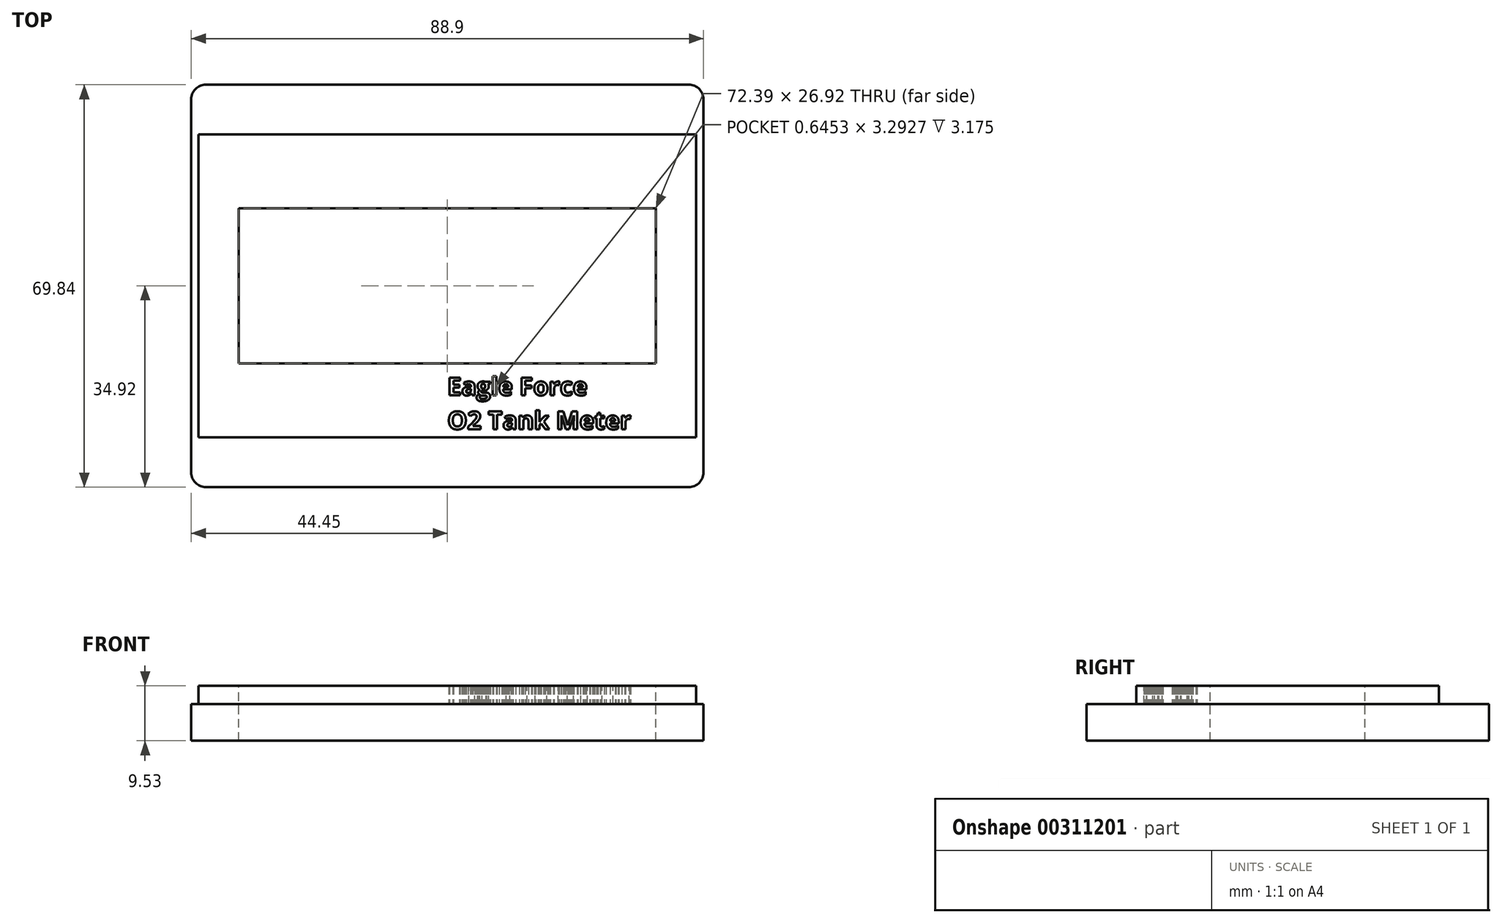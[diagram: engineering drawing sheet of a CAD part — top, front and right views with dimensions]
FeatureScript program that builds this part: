
annotation { "Feature Type Name" : "Feature", "Feature Type Description" : "" }
export const myFeature = defineFeature(function(context is Context, id is Id, definition is map)
    precondition{}
    {
        {
            var Q0;
            Q0=qCreatedBy(makeId("Top.planeOp"),FACE);
            var sketch = newSketch(context, id + "F0", { "sketchPlane" : qUnion([Q0])});
            skLineSegment(sketch, "E0.bottom", {"start": v(-44.45, 34.93) * mm, "end": v(44.45, 34.93) * mm});
            skLineSegment(sketch, "E0.top", {"start": v(-44.45, -34.93) * mm, "end": v(44.45, -34.93) * mm});
            skLineSegment(sketch, "E0.left", {"start": v(-44.45, 34.93) * mm, "end": v(-44.45, -34.93) * mm});
            skLineSegment(sketch, "E0.right", {"start": v(44.45, 34.93) * mm, "end": v(44.45, -34.93) * mm});
            skPoint(sketch, "E0.middle", {"position": v(0, 0) * mm});
            skSolve(sketch);
        }
        {
            var Q0;
            Q0 = qSketchRegion(id + "F0", true);
            extrude(context, id + "F1", {"entities" : qUnion([Q0]), "depth" : 6.35 * mm});
        }
        {
            var Q0;
            Q0=makeQuery(id+"F1.opExtrude","CAP_FACE",FACE,{"disambiguationData":[OSD([sQuery(id+"F0.wireOp",EDGE,"E0.bottom"),sQuery(id+"F0.wireOp",EDGE,"E0.top"),sQuery(id+"F0.wireOp",EDGE,"E0.left"),sQuery(id+"F0.wireOp",EDGE,"E0.right")])],"isStart":false});
            var sketch = newSketch(context, id + "F2", { "sketchPlane" : qUnion([Q0])});
            skLineSegment(sketch, "E1", {"start": v(0, 0) * mm, "end": v(-38.8, 0) * mm});
            skLineSegment(sketch, "E2", {"start": v(-38.8, 0) * mm, "end": v(-38.8, 16.79) * mm});
            skSolve(sketch);
        }
        {
            var Q0;
            Q0=makeQuery(id+"F1.opExtrude","SWEPT_BODY",BODY,{"disambiguationData":[OSD([sQuery(id+"F0.wireOp",EDGE,"E0.bottom"),sQuery(id+"F0.wireOp",EDGE,"E0.top"),sQuery(id+"F0.wireOp",EDGE,"E0.left"),sQuery(id+"F0.wireOp",EDGE,"E0.right")])]});
            var Q1;
            Q1=qCreatedBy(makeId("Front.planeOp"),FACE);
            mirror(context, id + "F3", {"operationType" : NewBodyOperationType.ADD, "entities" : qUnion([Q0]), "mirrorPlane" : qUnion([Q1])});
        }
        {
            var Q0;
            Q0=makeQuery(id+"F1.opExtrude","SWEPT_BODY",BODY,{"disambiguationData":[OSD([sQuery(id+"F0.wireOp",EDGE,"E0.bottom"),sQuery(id+"F0.wireOp",EDGE,"E0.top"),sQuery(id+"F0.wireOp",EDGE,"E0.left"),sQuery(id+"F0.wireOp",EDGE,"E0.right")])]});
            var Q1;
            Q1=qCreatedBy(makeId("Right.planeOp"),FACE);
            mirror(context, id + "F4", {"operationType" : NewBodyOperationType.ADD, "entities" : qUnion([Q0]), "mirrorPlane" : qUnion([Q1])});
        }
        {
            var Q0;
            Q0=makeQuery(id+"F2.imprint","IMPRINT",FACE,{"disambiguationData":[TD([[makeQuery(id+"F2.imprint","IMPRINT",EDGE,{"derivedFrom":makeQuery(id+"F1.opExtrude","CAP_EDGE",EDGE,{"disambiguationData":[OSD([sQuery(id+"F0.wireOp",EDGE,"E0.bottom")])],"isStart":false})}),-1.0]])]});
            var sketch = newSketch(context, id + "F5", { "sketchPlane" : qUnion([Q0])});
            skLineSegment(sketch, "E3.bottom", {"start": v(-36.2, 13.46) * mm, "end": v(36.2, 13.46) * mm});
            skLineSegment(sketch, "E3.top", {"start": v(-36.2, -13.46) * mm, "end": v(36.2, -13.46) * mm});
            skLineSegment(sketch, "E3.left", {"start": v(-36.2, 13.46) * mm, "end": v(-36.2, -13.46) * mm});
            skLineSegment(sketch, "E3.right", {"start": v(36.2, 13.46) * mm, "end": v(36.2, -13.46) * mm});
            skPoint(sketch, "E3.middle", {"position": v(0, 0) * mm});
            skSolve(sketch);
        }
        {
            var Q0;
            Q0=makeQuery(id+"F1.opExtrude","SWEPT_EDGE",EDGE,{"disambiguationData":[OSD([sQuery(id+"F0.wireOp",EDGE,"E0.bottom"),sQuery(id+"F0.wireOp",EDGE,"E0.right")])]});
            var Q1;
            Q1=makeQuery(id+"F1.opExtrude","SWEPT_EDGE",EDGE,{"disambiguationData":[OSD([sQuery(id+"F0.wireOp",EDGE,"E0.bottom"),sQuery(id+"F0.wireOp",EDGE,"E0.left")])]});
            var Q2;
            Q2=makeQuery(id+"F1.opExtrude","SWEPT_EDGE",EDGE,{"disambiguationData":[OSD([sQuery(id+"F0.wireOp",EDGE,"E0.top"),sQuery(id+"F0.wireOp",EDGE,"E0.left")])]});
            var Q3;
            Q3=makeQuery(id+"F1.opExtrude","SWEPT_EDGE",EDGE,{"disambiguationData":[OSD([sQuery(id+"F0.wireOp",EDGE,"E0.top"),sQuery(id+"F0.wireOp",EDGE,"E0.right")])]});
            fillet(context, id + "F6", {"entities" : qUnion([Q0, Q1, Q2, Q3]), "radius" : 2.54 * mm, "tangentPropagation" : true, "allowEdgeOverflow" : false});
        }
        {
            var Q0;
            Q0=makeQuery(id+"F2.imprint","IMPRINT",FACE,{"disambiguationData":[TD([[makeQuery(id+"F2.imprint","IMPRINT",EDGE,{"derivedFrom":makeQuery(id+"F1.opExtrude","CAP_EDGE",EDGE,{"disambiguationData":[OSD([sQuery(id+"F0.wireOp",EDGE,"E0.bottom")])],"isStart":false})}),-1.0]])]});
            var sketch = newSketch(context, id + "F7", { "sketchPlane" : qUnion([Q0])});
            skLineSegment(sketch, "E4.bottom", {"start": v(43.18, 26.28) * mm, "end": v(-43.18, 26.28) * mm});
            skLineSegment(sketch, "E4.top", {"start": v(43.18, -26.28) * mm, "end": v(-43.18, -26.28) * mm});
            skLineSegment(sketch, "E4.left", {"start": v(43.18, 26.28) * mm, "end": v(43.18, -26.28) * mm});
            skLineSegment(sketch, "E4.right", {"start": v(-43.18, 26.28) * mm, "end": v(-43.18, -26.28) * mm});
            skPoint(sketch, "E4.middle", {"position": v(0, 0) * mm});
            skSolve(sketch);
        }
        {
            var Q0;
            Q0 = qSketchRegion(id + "F7", true);
            extrude(context, id + "F8", {"entities" : qUnion([Q0]), "operationType" : NewBodyOperationType.ADD, "depth" : 3.17 * mm});
        }
        {
            var Q0;
            Q0 = qSketchRegion(id + "F5", true);
            extrude(context, id + "F9", {"entities" : qUnion([Q0]), "operationType" : NewBodyOperationType.REMOVE, "oppositeDirection" : true, "depth" : 25.4 * mm, "hasSecondDirection" : true, "secondDirectionBound" : SecondDirectionBoundingType.THROUGH_ALL, "secondDirectionOppositeDirection" : false, "secondDirectionDepth" : 25.4 * mm});
        }
        {
            var Q0;
            Q0=makeQuery(id+"F5.imprint","IMPRINT",FACE,{"disambiguationData":[TD([[makeQuery(id+"F5.imprint","IMPRINT",EDGE,{"derivedFrom":sQuery(id+"F5.wireOp",EDGE,"E3.bottom")}),1.0]])]});
            var sketch = newSketch(context, id + "F10", { "sketchPlane" : qUnion([Q0])});
            skText(sketch, "E5", { "text": "Eagle Force\nO2 Tank Meter\nV1.0", "fontName": "OpenSans-Bold.ttf"});
            const initialGuessF10  = {"E5": [0, -0.019, 1, 0, 0.00312]};
            skSetInitialGuess(sketch, initialGuessF10);
            skSolve(sketch);
        }
        {
            var Q0;
            Q0 = qSketchRegion(id + "F10", true);
            extrude(context, id + "F11", {"entities" : qUnion([Q0]), "operationType" : NewBodyOperationType.REMOVE, "depth" : 6.35 * mm});
        }
    });
